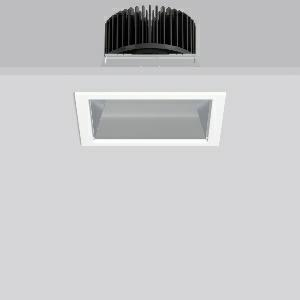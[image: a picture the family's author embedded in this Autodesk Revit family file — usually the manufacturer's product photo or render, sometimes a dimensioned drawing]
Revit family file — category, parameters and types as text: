
# Revit family: quardo_901705_002_76_796c
name_source: partatom
category: Lighting Fixtures
units: mm (PartAtom-declared; Revit-internal decimal feet)

## family parameters
Cut with Voids When Loaded = No
Host = Face
Light Source = No
Part Type = Normal
Room Calculation Point = No
Round Connector Dimension = Use Diameter
Shared = No

## types (1)
- QUARDO (1 x LED Modul 830, 2500 lm, 3000)
    Apparent Load = 19 VA
    CIE Flux Codes = 80 100 100 100 100
    Color Rendering = 80
    Color Temperature = 3000
    Default Elevation = 1800 mm
    Description = Series: QUARDO
High-quality recessed downlight with square luminous surface. Recessed mounting frame: die-cast aluminium, powder-coated. Mounting bracket: galvanised sheet steel. Reflector: aluminium, highly polished anodised finish. Ceiling installation with spring system. Including separate LED converter with connecting cable 600 mm. Through-wiring box (5 pole) available as accessory. 
Colour: traffic white, matt (RAL 9016)
Length: 176 mm
Width: 176 mm
Height: 4 mm
Cut-out length: 165 mm
Cut-out width: 165 mm
Recess height: 150 mm
Luminaire: recess height: 145 mm
Lamp: LED
Socket: without socket
Colour temperature: 3000K
Colour rendering index (CRI): 85
System power: 19 W
Rated luminous flux: 2500 lm
Luminous efficiency: 132 lm/W
Control gear: Converter, dimmable, DALI
Protection class: II
Type of protection: IP 20
    Height = 0 mm  [stored 0 ft]
    Lamp = 1 x LED Modul 830
    Lamp Light Flux = 2500 lm
    Lamp count = 1
    Length = 176 mm
    Lifetime = 50000 h
    Luminous efficacy = 132 lm/W
    Manufacturer = RZB
    ModVariant = No
    Model = 901705.002.76
    Mounting Place = Ceiling
    Mounting Type = Recessed
    Number of Poles = 1
    OnlyDefault = Yes
    Power Factor = 1
    Product Name = QUARDO
    Product group = Recessed downlights
    ProductGroupID = 402
    Protection Class = Protection class II
    Protection Degree = IP 20
    RLX_Detail_Level = 1
    RLX_Emergency_Light_Flux = 0 lm
    RLX_Emergency_Type = 0
    RLX_Emergency_Type_DB = No
    RlxData = <blob elided: 29301 chars, md5=d1c53733>
    Socket = socket
    Standby Power = 0 W
    System Light Flux = 2500 lm
    System Power = 19 W
    Type Comments = Product without accessories
    Type Image = 901705.002.jpg
    URL = http://relux.com
    VarID = ---
    Voltage = 230 V
    Voltage Range = 220-240 V
    Weight = 0.00 kg
    Width = 176 mm

note: [stored X ft] marks values corroborated as IEEE doubles in the binary element streams (Revit-internal decimal feet)

## geometry (parser evidence)
native form markers: Blend x4, Sweep x13
no freeform markers — native parametric forms only
